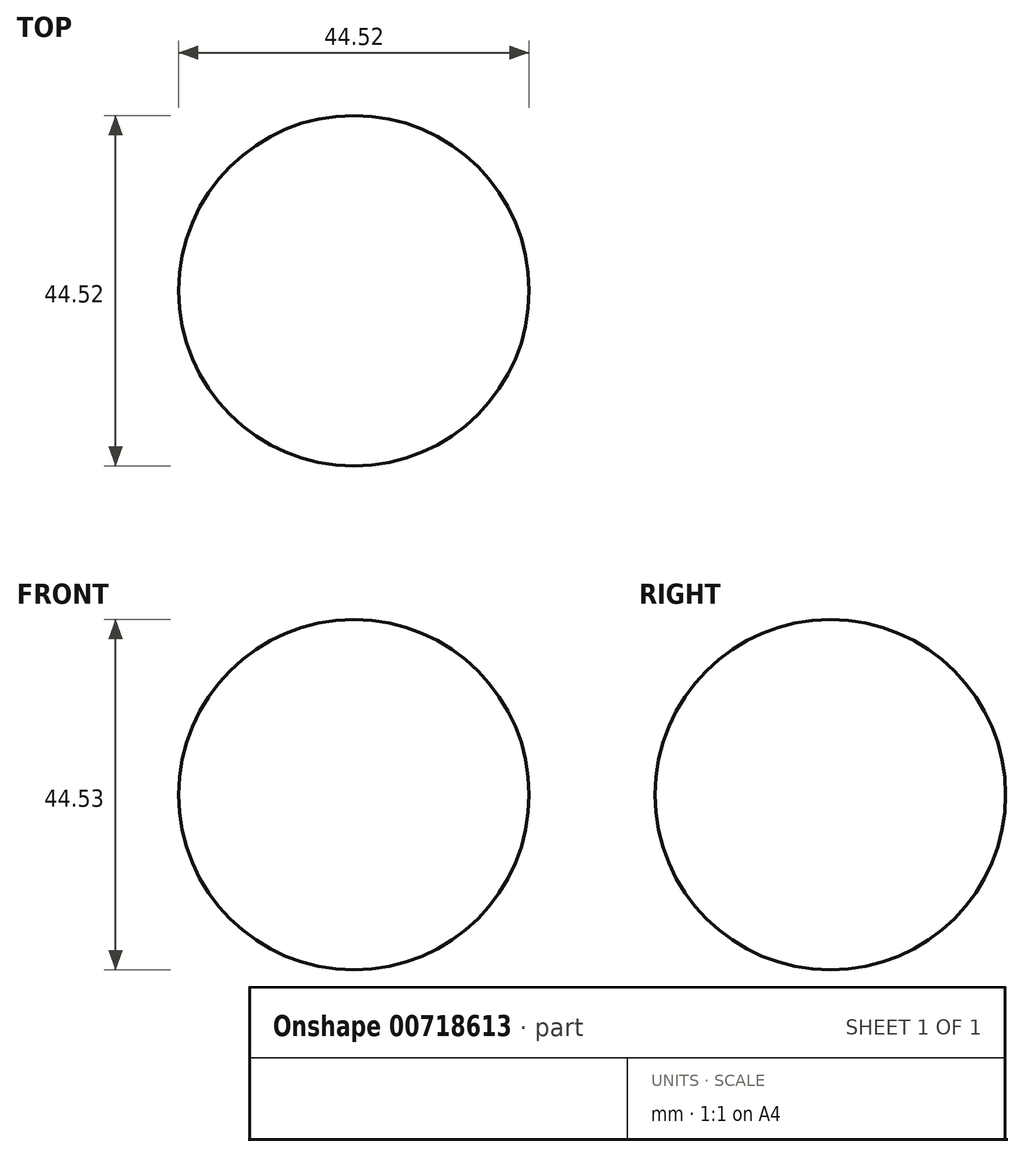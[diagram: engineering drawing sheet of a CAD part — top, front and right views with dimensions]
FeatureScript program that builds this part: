
annotation { "Feature Type Name" : "Feature", "Feature Type Description" : "" }
export const myFeature = defineFeature(function(context is Context, id is Id, definition is map)
    precondition{}
    {
        {
            var Q0;
            Q0=qCreatedBy(makeId("Front.planeOp"),FACE);
            var sketch = newSketch(context, id + "F0", { "sketchPlane" : qUnion([Q0])});
            skArc(sketch, "E0", {"start": v(22.26, 22.26) * mm, "mid": v(0, 44.53) * mm, "end": v(-22.26, 22.26) * mm});
            skLineSegment(sketch, "E1", {"start": v(22.26, 22.26) * mm, "end": v(4.84, 22.26) * mm});
            skLineSegment(sketch, "E2", {"start": v(-22.26, 22.26) * mm, "end": v(4.84, 22.26) * mm});
            skSolve(sketch);
        }
        {
            var Q0;
            Q0=makeQuery(id+"F0.imprint","IMPRINT",FACE,{"disambiguationData":[TD([[makeQuery(id+"F0.imprint","IMPRINT",EDGE,{"derivedFrom":sQuery(id+"F0.wireOp",EDGE,"E0")}),1.0]])]});
            var sketch = newSketch(context, id + "F1", { "sketchPlane" : qUnion([Q0])});
            skSolve(sketch);
        }
        {
            var Q0;
            Q0=makeQuery(id+"F1.imprint","IMPRINT",FACE,{"disambiguationData":[TD([[makeQuery(id+"F1.imprint","IMPRINT",EDGE,{"derivedFrom":makeQuery(id+"F0.imprint","IMPRINT",EDGE,{"derivedFrom":sQuery(id+"F0.wireOp",EDGE,"E0")})}),1.0]])]});
            var Q1;
            Q1=sQuery(id+"F0.wireOp",EDGE,"E2");
            revolve(context, id + "F2", {"surfaceOperationType" : NewSurfaceOperationType.NEW, "entities" : qUnion([Q0]), "axis" : qUnion([Q1]), "revolveType" : RevolveType.FULL});
        }
    });
